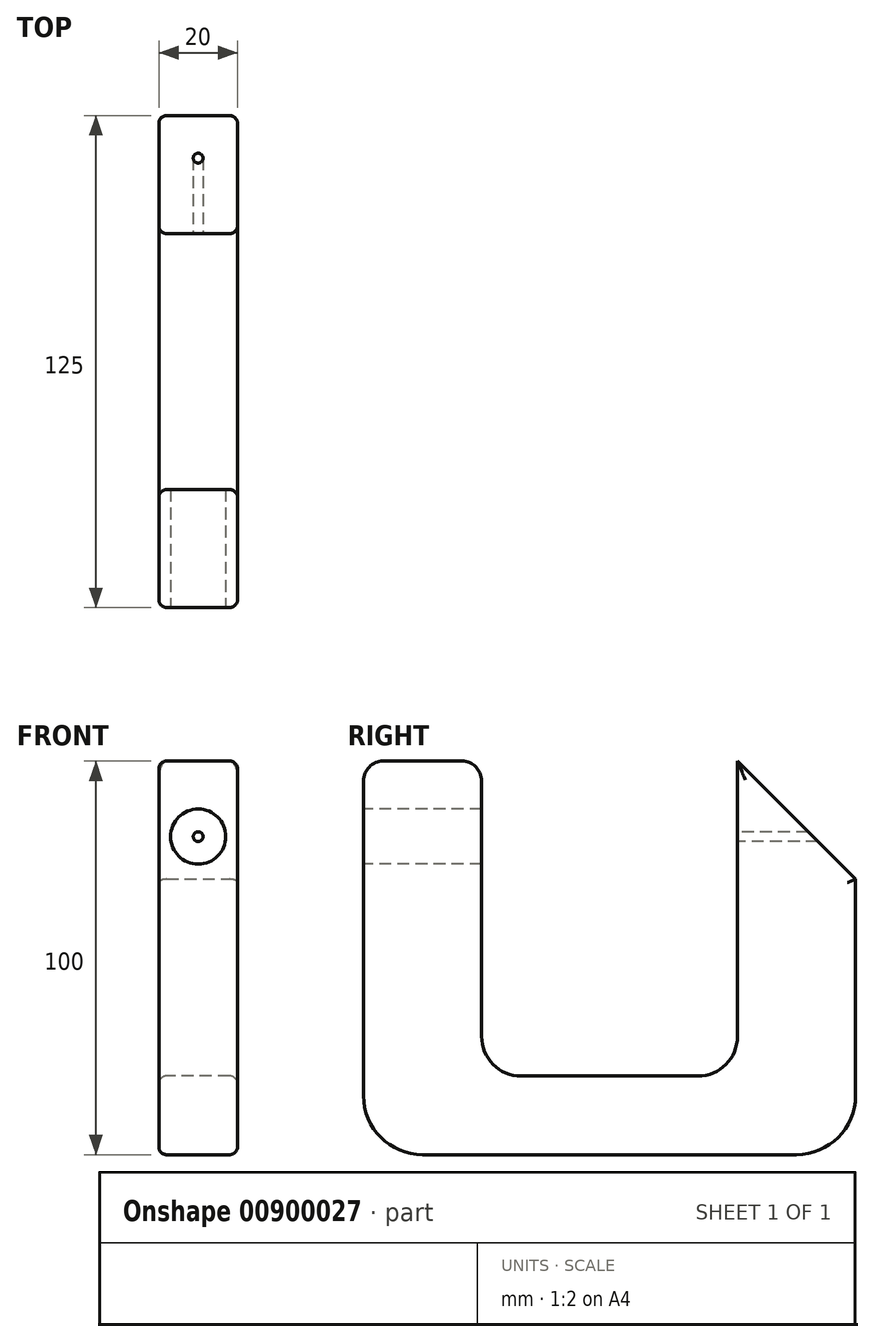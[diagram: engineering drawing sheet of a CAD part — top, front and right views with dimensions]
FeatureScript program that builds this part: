
annotation { "Feature Type Name" : "Feature", "Feature Type Description" : "" }
export const myFeature = defineFeature(function(context is Context, id is Id, definition is map)
    precondition{}
    {
        {
            var Q0;
            Q0=qCreatedBy(makeId("Right.planeOp"),FACE);
            var sketch = newSketch(context, id + "F0", { "sketchPlane" : qUnion([Q0])});
            skLineSegment(sketch, "E0.top", {"start": v(0, -100) * mm, "end": v(125, -100) * mm});
            skLineSegment(sketch, "E0.left", {"start": v(0, 0) * mm, "end": v(0, -100) * mm});
            skLineSegment(sketch, "E0.right", {"start": v(125, 0) * mm, "end": v(125, -100) * mm});
            skLineSegment(sketch, "E1", {"start": v(125, 0) * mm, "end": v(95, 0) * mm});
            skLineSegment(sketch, "E2", {"start": v(95, 0) * mm, "end": v(95, -100) * mm});
            skLineSegment(sketch, "E3", {"start": v(95, -100) * mm, "end": v(95, -80) * mm});
            skLineSegment(sketch, "E4", {"start": v(95, -80) * mm, "end": v(125, -80) * mm});
            skLineSegment(sketch, "E5", {"start": v(125, -80) * mm, "end": v(0, -80) * mm});
            skLineSegment(sketch, "E6", {"start": v(30, -80) * mm, "end": v(30, -100) * mm});
            skLineSegment(sketch, "E7", {"start": v(30, -100) * mm, "end": v(30, 0) * mm});
            skLineSegment(sketch, "E8", {"start": v(30, 0) * mm, "end": v(0, 0) * mm});
            skSolve(sketch);
        }
        {
            var Q0;
            Q0 = qSketchRegion(id + "F0", true);
            extrude(context, id + "F1", {"entities" : qUnion([Q0]), "depth" : 20 * mm, "offsetDistance" : 25 * mm});
        }
        {
            var Q0;
            Q0=makeQuery(id+"F1.opExtrude","SWEPT_EDGE",EDGE,{"disambiguationData":[OSD([sQuery(id+"F0.wireOp",EDGE,"E2"),sQuery(id+"F0.wireOp",EDGE,"E3"),sQuery(id+"F0.wireOp",EDGE,"E5")])]});
            var Q1;
            Q1=makeQuery(id+"F1.opExtrude","SWEPT_EDGE",EDGE,{"disambiguationData":[OSD([sQuery(id+"F0.wireOp",EDGE,"E5"),sQuery(id+"F0.wireOp",EDGE,"E7")])]});
            fillet(context, id + "F2", {"entities" : qUnion([Q0, Q1]), "radius" : 10 * mm, "tangentPropagation" : true, "allowEdgeOverflow" : false});
        }
        {
            var Q0;
            Q0=makeQuery(id+"F1.opExtrude","SWEPT_EDGE",EDGE,{"disambiguationData":[OSD([sQuery(id+"F0.wireOp",EDGE,"E0.right"),sQuery(id+"F0.wireOp",EDGE,"E1")])]});
            chamfer(context, id + "F3", {"entities" : qUnion([Q0]), "width" : 30 * mm, "tangentPropagation" : true});
        }
        {
            var Q0;
            {var subQ0=sQuery(id+"F0.wireOp",EDGE,"E5");var subQ1=sQuery(id+"F0.wireOp",EDGE,"E2");Q0=makeQuery(id+"F2.opFillet","BLEND_EDGE",EDGE,{"blendedFrom":[makeQuery(id+"F1.opExtrude","SWEPT_EDGE",EDGE,{"disambiguationData":[OSD([subQ1,sQuery(id+"F0.wireOp",EDGE,"E3"),subQ0])]}),makeQuery(id+"F1.opExtrude","CAP_FACE",FACE,{"disambiguationData":[OSD([sQuery(id+"F0.wireOp",EDGE,"E0.top"),sQuery(id+"F0.wireOp",EDGE,"E0.left"),sQuery(id+"F0.wireOp",EDGE,"E0.right"),sQuery(id+"F0.wireOp",EDGE,"E1"),subQ1,subQ0,sQuery(id+"F0.wireOp",EDGE,"E7"),sQuery(id+"F0.wireOp",EDGE,"E8")])],"isStart":false})],"blendedInto":[makeQuery(id+"F1.opExtrude","CAP_FACE",FACE,{"disambiguationData":[OSD([sQuery(id+"F0.wireOp",EDGE,"E0.top"),sQuery(id+"F0.wireOp",EDGE,"E0.left"),sQuery(id+"F0.wireOp",EDGE,"E0.right"),sQuery(id+"F0.wireOp",EDGE,"E1"),subQ1,subQ0,sQuery(id+"F0.wireOp",EDGE,"E7"),sQuery(id+"F0.wireOp",EDGE,"E8")])],"isStart":false})]});}
            var Q1;
            Q1=makeQuery(id+"F1.opExtrude","CAP_EDGE",EDGE,{"disambiguationData":[OSD([sQuery(id+"F0.wireOp",EDGE,"E2")])],"isStart":false});
            var Q2;
            {var subQ0=sQuery(id+"F0.wireOp",EDGE,"E1");var subQ1=sQuery(id+"F0.wireOp",EDGE,"E0.right");Q2=makeQuery(id+"F3.opChamfer","BLEND_EDGE",EDGE,{"blendedFrom":[makeQuery(id+"F1.opExtrude","SWEPT_EDGE",EDGE,{"disambiguationData":[OSD([subQ1,subQ0])]}),makeQuery(id+"F1.opExtrude","CAP_FACE",FACE,{"disambiguationData":[OSD([sQuery(id+"F0.wireOp",EDGE,"E0.top"),sQuery(id+"F0.wireOp",EDGE,"E0.left"),subQ1,subQ0,sQuery(id+"F0.wireOp",EDGE,"E2"),sQuery(id+"F0.wireOp",EDGE,"E5"),sQuery(id+"F0.wireOp",EDGE,"E7"),sQuery(id+"F0.wireOp",EDGE,"E8")])],"isStart":false})],"blendedInto":[makeQuery(id+"F1.opExtrude","CAP_FACE",FACE,{"disambiguationData":[OSD([sQuery(id+"F0.wireOp",EDGE,"E0.top"),sQuery(id+"F0.wireOp",EDGE,"E0.left"),subQ1,subQ0,sQuery(id+"F0.wireOp",EDGE,"E2"),sQuery(id+"F0.wireOp",EDGE,"E5"),sQuery(id+"F0.wireOp",EDGE,"E7"),sQuery(id+"F0.wireOp",EDGE,"E8")])],"isStart":false})]});}
            var Q3;
            Q3=makeQuery(id+"F1.opExtrude","CAP_EDGE",EDGE,{"disambiguationData":[OSD([sQuery(id+"F0.wireOp",EDGE,"E0.right")])],"isStart":false});
            var Q4;
            Q4=makeQuery(id+"F1.opExtrude","CAP_EDGE",EDGE,{"disambiguationData":[OSD([sQuery(id+"F0.wireOp",EDGE,"E0.top")])],"isStart":false});
            var Q5;
            Q5=makeQuery(id+"F1.opExtrude","CAP_EDGE",EDGE,{"disambiguationData":[OSD([sQuery(id+"F0.wireOp",EDGE,"E0.left")])],"isStart":false});
            var Q6;
            Q6=makeQuery(id+"F1.opExtrude","CAP_EDGE",EDGE,{"disambiguationData":[OSD([sQuery(id+"F0.wireOp",EDGE,"E8")])],"isStart":false});
            var Q7;
            Q7=makeQuery(id+"F1.opExtrude","CAP_EDGE",EDGE,{"disambiguationData":[OSD([sQuery(id+"F0.wireOp",EDGE,"E7")])],"isStart":false});
            var Q8;
            {var subQ0=sQuery(id+"F0.wireOp",EDGE,"E7");var subQ1=sQuery(id+"F0.wireOp",EDGE,"E5");Q8=makeQuery(id+"F2.opFillet","BLEND_EDGE",EDGE,{"blendedFrom":[makeQuery(id+"F1.opExtrude","SWEPT_EDGE",EDGE,{"disambiguationData":[OSD([subQ1,subQ0])]}),makeQuery(id+"F1.opExtrude","CAP_FACE",FACE,{"disambiguationData":[OSD([sQuery(id+"F0.wireOp",EDGE,"E0.top"),sQuery(id+"F0.wireOp",EDGE,"E0.left"),sQuery(id+"F0.wireOp",EDGE,"E0.right"),sQuery(id+"F0.wireOp",EDGE,"E1"),sQuery(id+"F0.wireOp",EDGE,"E2"),subQ1,subQ0,sQuery(id+"F0.wireOp",EDGE,"E8")])],"isStart":false})],"blendedInto":[makeQuery(id+"F1.opExtrude","CAP_FACE",FACE,{"disambiguationData":[OSD([sQuery(id+"F0.wireOp",EDGE,"E0.top"),sQuery(id+"F0.wireOp",EDGE,"E0.left"),sQuery(id+"F0.wireOp",EDGE,"E0.right"),sQuery(id+"F0.wireOp",EDGE,"E1"),sQuery(id+"F0.wireOp",EDGE,"E2"),subQ1,subQ0,sQuery(id+"F0.wireOp",EDGE,"E8")])],"isStart":false})]});}
            var Q9;
            Q9=makeQuery(id+"F1.opExtrude","CAP_EDGE",EDGE,{"disambiguationData":[OSD([sQuery(id+"F0.wireOp",EDGE,"E5")])],"isStart":false});
            fillet(context, id + "F4", {"entities" : qUnion([Q0, Q1, Q2, Q3, Q4, Q5, Q6, Q7, Q8, Q9]), "radius" : 2 * mm, "tangentPropagation" : true, "allowEdgeOverflow" : false});
        }
        {
            var Q0;
            Q0=makeQuery(id+"F1.opExtrude","CAP_EDGE",EDGE,{"disambiguationData":[OSD([sQuery(id+"F0.wireOp",EDGE,"E8")])],"isStart":true});
            var Q1;
            Q1=makeQuery(id+"F1.opExtrude","CAP_EDGE",EDGE,{"disambiguationData":[OSD([sQuery(id+"F0.wireOp",EDGE,"E0.left")])],"isStart":true});
            var Q2;
            Q2=makeQuery(id+"F1.opExtrude","CAP_EDGE",EDGE,{"disambiguationData":[OSD([sQuery(id+"F0.wireOp",EDGE,"E7")])],"isStart":true});
            var Q3;
            {var subQ0=sQuery(id+"F0.wireOp",EDGE,"E7");var subQ1=sQuery(id+"F0.wireOp",EDGE,"E5");Q3=makeQuery(id+"F2.opFillet","BLEND_EDGE",EDGE,{"blendedFrom":[makeQuery(id+"F1.opExtrude","SWEPT_EDGE",EDGE,{"disambiguationData":[OSD([subQ1,subQ0])]}),makeQuery(id+"F1.opExtrude","CAP_FACE",FACE,{"disambiguationData":[OSD([sQuery(id+"F0.wireOp",EDGE,"E0.top"),sQuery(id+"F0.wireOp",EDGE,"E0.left"),sQuery(id+"F0.wireOp",EDGE,"E0.right"),sQuery(id+"F0.wireOp",EDGE,"E1"),sQuery(id+"F0.wireOp",EDGE,"E2"),subQ1,subQ0,sQuery(id+"F0.wireOp",EDGE,"E8")])],"isStart":true})],"blendedInto":[makeQuery(id+"F1.opExtrude","CAP_FACE",FACE,{"disambiguationData":[OSD([sQuery(id+"F0.wireOp",EDGE,"E0.top"),sQuery(id+"F0.wireOp",EDGE,"E0.left"),sQuery(id+"F0.wireOp",EDGE,"E0.right"),sQuery(id+"F0.wireOp",EDGE,"E1"),sQuery(id+"F0.wireOp",EDGE,"E2"),subQ1,subQ0,sQuery(id+"F0.wireOp",EDGE,"E8")])],"isStart":true})]});}
            var Q4;
            Q4=makeQuery(id+"F1.opExtrude","CAP_EDGE",EDGE,{"disambiguationData":[OSD([sQuery(id+"F0.wireOp",EDGE,"E5")])],"isStart":true});
            var Q5;
            {var subQ0=sQuery(id+"F0.wireOp",EDGE,"E5");var subQ1=sQuery(id+"F0.wireOp",EDGE,"E2");Q5=makeQuery(id+"F2.opFillet","BLEND_EDGE",EDGE,{"blendedFrom":[makeQuery(id+"F1.opExtrude","SWEPT_EDGE",EDGE,{"disambiguationData":[OSD([subQ1,sQuery(id+"F0.wireOp",EDGE,"E3"),subQ0])]}),makeQuery(id+"F1.opExtrude","CAP_FACE",FACE,{"disambiguationData":[OSD([sQuery(id+"F0.wireOp",EDGE,"E0.top"),sQuery(id+"F0.wireOp",EDGE,"E0.left"),sQuery(id+"F0.wireOp",EDGE,"E0.right"),sQuery(id+"F0.wireOp",EDGE,"E1"),subQ1,subQ0,sQuery(id+"F0.wireOp",EDGE,"E7"),sQuery(id+"F0.wireOp",EDGE,"E8")])],"isStart":true})],"blendedInto":[makeQuery(id+"F1.opExtrude","CAP_FACE",FACE,{"disambiguationData":[OSD([sQuery(id+"F0.wireOp",EDGE,"E0.top"),sQuery(id+"F0.wireOp",EDGE,"E0.left"),sQuery(id+"F0.wireOp",EDGE,"E0.right"),sQuery(id+"F0.wireOp",EDGE,"E1"),subQ1,subQ0,sQuery(id+"F0.wireOp",EDGE,"E7"),sQuery(id+"F0.wireOp",EDGE,"E8")])],"isStart":true})]});}
            var Q6;
            Q6=makeQuery(id+"F1.opExtrude","CAP_EDGE",EDGE,{"disambiguationData":[OSD([sQuery(id+"F0.wireOp",EDGE,"E2")])],"isStart":true});
            var Q7;
            {var subQ0=sQuery(id+"F0.wireOp",EDGE,"E1");var subQ1=sQuery(id+"F0.wireOp",EDGE,"E0.right");Q7=makeQuery(id+"F3.opChamfer","BLEND_EDGE",EDGE,{"blendedFrom":[makeQuery(id+"F1.opExtrude","SWEPT_EDGE",EDGE,{"disambiguationData":[OSD([subQ1,subQ0])]}),makeQuery(id+"F1.opExtrude","CAP_FACE",FACE,{"disambiguationData":[OSD([sQuery(id+"F0.wireOp",EDGE,"E0.top"),sQuery(id+"F0.wireOp",EDGE,"E0.left"),subQ1,subQ0,sQuery(id+"F0.wireOp",EDGE,"E2"),sQuery(id+"F0.wireOp",EDGE,"E5"),sQuery(id+"F0.wireOp",EDGE,"E7"),sQuery(id+"F0.wireOp",EDGE,"E8")])],"isStart":true})],"blendedInto":[makeQuery(id+"F1.opExtrude","CAP_FACE",FACE,{"disambiguationData":[OSD([sQuery(id+"F0.wireOp",EDGE,"E0.top"),sQuery(id+"F0.wireOp",EDGE,"E0.left"),subQ1,subQ0,sQuery(id+"F0.wireOp",EDGE,"E2"),sQuery(id+"F0.wireOp",EDGE,"E5"),sQuery(id+"F0.wireOp",EDGE,"E7"),sQuery(id+"F0.wireOp",EDGE,"E8")])],"isStart":true})]});}
            var Q8;
            Q8=makeQuery(id+"F1.opExtrude","CAP_EDGE",EDGE,{"disambiguationData":[OSD([sQuery(id+"F0.wireOp",EDGE,"E0.right")])],"isStart":true});
            var Q9;
            Q9=makeQuery(id+"F1.opExtrude","CAP_EDGE",EDGE,{"disambiguationData":[OSD([sQuery(id+"F0.wireOp",EDGE,"E0.top")])],"isStart":true});
            fillet(context, id + "F5", {"entities" : qUnion([Q0, Q1, Q2, Q3, Q4, Q5, Q6, Q7, Q8, Q9]), "radius" : 2 * mm, "tangentPropagation" : true, "allowEdgeOverflow" : false});
        }
        {
            var Q0;
            Q0=makeQuery(id+"F1.opExtrude","SWEPT_EDGE",EDGE,{"disambiguationData":[OSD([sQuery(id+"F0.wireOp",EDGE,"E0.left"),sQuery(id+"F0.wireOp",EDGE,"E8")])]});
            fillet(context, id + "F6", {"entities" : qUnion([Q0]), "radius" : 5 * mm, "tangentPropagation" : true, "allowEdgeOverflow" : false});
        }
        {
            var Q0;
            Q0=makeQuery(id+"F1.opExtrude","SWEPT_EDGE",EDGE,{"disambiguationData":[OSD([sQuery(id+"F0.wireOp",EDGE,"E0.top"),sQuery(id+"F0.wireOp",EDGE,"E0.left")])]});
            var Q1;
            Q1=makeQuery(id+"F1.opExtrude","SWEPT_EDGE",EDGE,{"disambiguationData":[OSD([sQuery(id+"F0.wireOp",EDGE,"E0.top"),sQuery(id+"F0.wireOp",EDGE,"E0.right")])]});
            fillet(context, id + "F7", {"entities" : qUnion([Q0, Q1]), "radius" : 15 * mm, "tangentPropagation" : true, "allowEdgeOverflow" : false});
        }
        {
            var Q0;
            Q0=makeQuery(id+"F1.opExtrude","SWEPT_FACE",FACE,{"disambiguationData":[OSD([sQuery(id+"F0.wireOp",EDGE,"E0.left")])]});
            var sketch = newSketch(context, id + "F8", { "sketchPlane" : qUnion([Q0])});
            skCircle(sketch, "E9", {"center": v(10, -19.19) * mm, "radius": 7 * mm});
            skPoint(sketch, "E9.centerSnap0", {"position": v(10, -5) * mm});
            skSolve(sketch);
        }
        {
            var Q0;
            Q0=makeQuery(id+"F8.imprint","IMPRINT",FACE,{"disambiguationData":[TD([[makeQuery(id+"F8.imprint","IMPRINT",EDGE,{"derivedFrom":sQuery(id+"F8.wireOp",EDGE,"E9")}),1.0]])]});
            extrude(context, id + "F9", {"entities" : qUnion([Q0]), "operationType" : NewBodyOperationType.REMOVE, "oppositeDirection" : true, "depth" : 52.5 * mm, "offsetDistance" : 25 * mm});
        }
        {
            var Q0;
            Q0=makeQuery(id+"F1.opExtrude","SWEPT_EDGE",EDGE,{"disambiguationData":[OSD([sQuery(id+"F0.wireOp",EDGE,"E7"),sQuery(id+"F0.wireOp",EDGE,"E8")])]});
            fillet(context, id + "F10", {"entities" : qUnion([Q0]), "radius" : 5 * mm, "tangentPropagation" : true, "allowEdgeOverflow" : false});
        }
        {
            var Q0;
            Q0=makeQuery(id+"F1.opExtrude","SWEPT_FACE",FACE,{"disambiguationData":[OSD([sQuery(id+"F0.wireOp",EDGE,"E2")])]});
            var sketch = newSketch(context, id + "F11", { "sketchPlane" : qUnion([Q0])});
            skCircle(sketch, "E10", {"center": v(9.99, -19.2) * mm, "radius": 1.25 * mm});
            skSolve(sketch);
        }
        {
            var Q0;
            Q0 = qSketchRegion(id + "F11", true);
            extrude(context, id + "F12", {"entities" : qUnion([Q0]), "operationType" : NewBodyOperationType.REMOVE, "oppositeDirection" : true, "depth" : 53 * mm, "offsetDistance" : 25 * mm});
        }
    });
